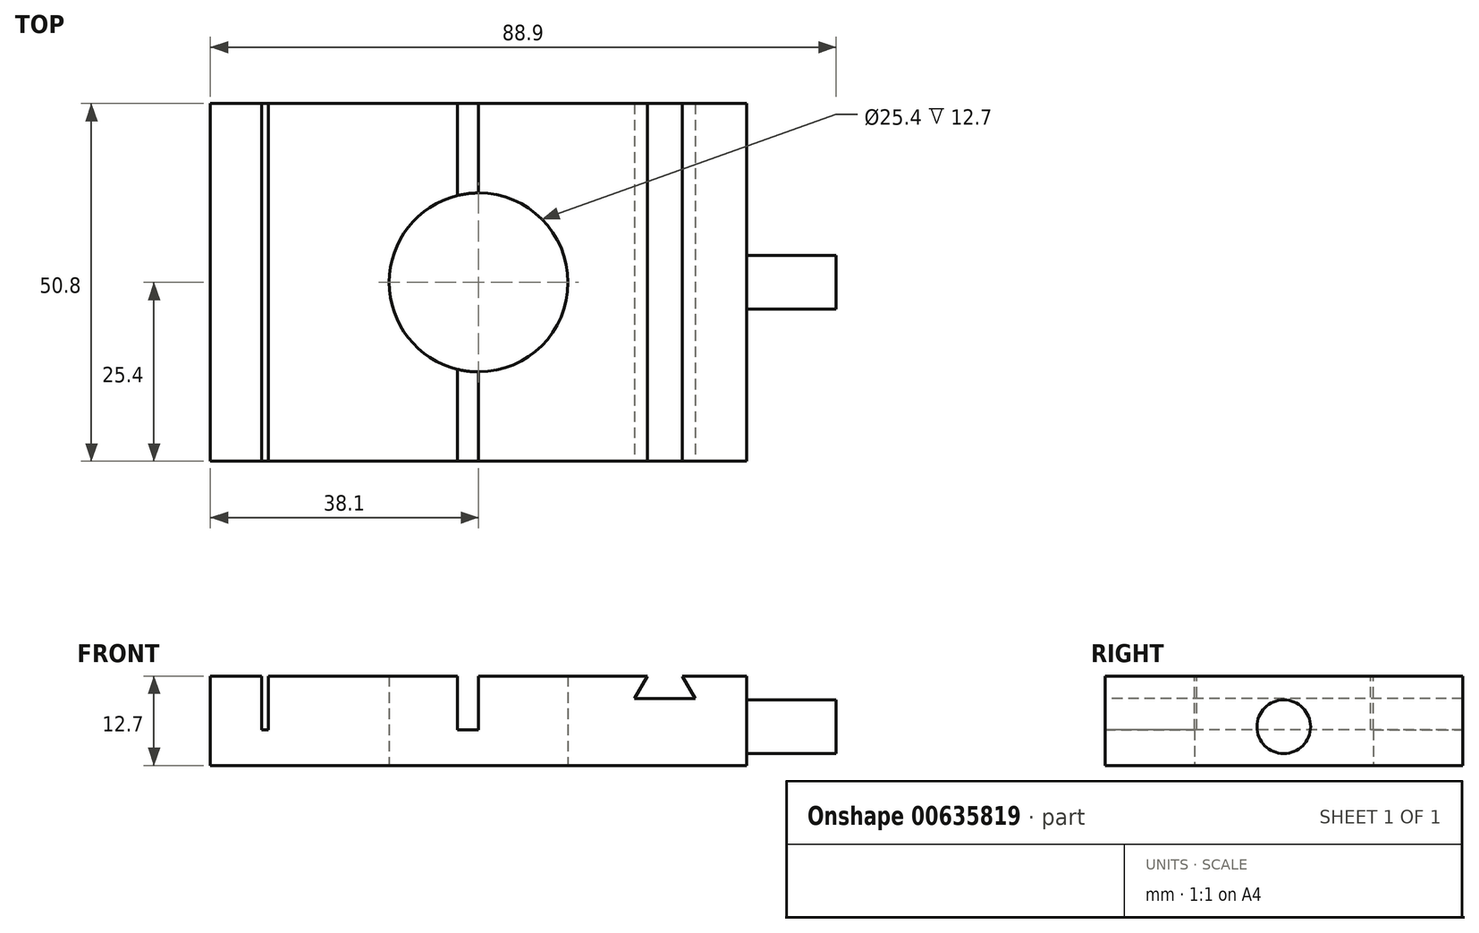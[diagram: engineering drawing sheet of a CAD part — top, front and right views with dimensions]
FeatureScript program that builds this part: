
annotation { "Feature Type Name" : "Feature", "Feature Type Description" : "" }
export const myFeature = defineFeature(function(context is Context, id is Id, definition is map)
    precondition{}
    {
        {
            var Q0;
            Q0=qCreatedBy(makeId("Top.planeOp"),FACE);
            var sketch = newSketch(context, id + "F0", { "sketchPlane" : qUnion([Q0])});
            skLineSegment(sketch, "E0.bottom", {"start": v(38.1, -25.4) * mm, "end": v(-38.1, -25.4) * mm});
            skLineSegment(sketch, "E0.top", {"start": v(38.1, 25.4) * mm, "end": v(-38.1, 25.4) * mm});
            skLineSegment(sketch, "E0.left", {"start": v(38.1, -25.4) * mm, "end": v(38.1, 25.4) * mm});
            skLineSegment(sketch, "E0.right", {"start": v(-38.1, -25.4) * mm, "end": v(-38.1, 25.4) * mm});
            skPoint(sketch, "E0.middle", {"position": v(0, 0) * mm});
            skCircle(sketch, "E1", {"center": v(0, 0) * mm, "radius": 12.7 * mm});
            skSolve(sketch);
        }
        {
            var Q0;
            Q0=makeQuery(id+"F0.imprint","IMPRINT",FACE,{"disambiguationData":[TD([[makeQuery(id+"F0.imprint","IMPRINT",EDGE,{"derivedFrom":sQuery(id+"F0.wireOp",EDGE,"E0.bottom")}),-1.0]])]});
            extrude(context, id + "F1", {"entities" : qUnion([Q0]), "depth" : 12.7 * mm, "offsetDistance" : 25.4 * mm});
        }
        {
            var Q0;
            Q0=makeQuery(id+"F1.opExtrude","CAP_FACE",FACE,{"disambiguationData":[OSD([sQuery(id+"F0.wireOp",EDGE,"E0.bottom"),sQuery(id+"F0.wireOp",EDGE,"E0.top"),sQuery(id+"F0.wireOp",EDGE,"E0.left"),sQuery(id+"F0.wireOp",EDGE,"E0.right"),sQuery(id+"F0.wireOp",EDGE,"E1")])],"isStart":false});
            var sketch = newSketch(context, id + "F2", { "sketchPlane" : qUnion([Q0])});
            skLineSegment(sketch, "E2", {"start": v(-30.83, 25.4) * mm, "end": v(-30.83, -25.4) * mm});
            skLineSegment(sketch, "E3", {"start": v(-30.83, -25.4) * mm, "end": v(-29.83, -25.4) * mm});
            skLineSegment(sketch, "E4", {"start": v(-29.83, -25.4) * mm, "end": v(-29.83, 25.4) * mm});
            skLineSegment(sketch, "E5", {"start": v(-29.83, 25.4) * mm, "end": v(-30.83, 25.4) * mm});
            skLineSegment(sketch, "E6", {"start": v(-3, 25.4) * mm, "end": v(-3, -25.4) * mm});
            skLineSegment(sketch, "E7", {"start": v(-3, -25.4) * mm, "end": v(0, -25.4) * mm});
            skLineSegment(sketch, "E8", {"start": v(0, -25.4) * mm, "end": v(0, 25.4) * mm});
            skLineSegment(sketch, "E9", {"start": v(0, 25.4) * mm, "end": v(-3, 25.4) * mm});
            skLineSegment(sketch, "E10", {"start": v(-30.33, 25.4) * mm, "end": v(-30.33, -25.4) * mm, "construction": true});
            skLineSegment(sketch, "E11", {"start": v(-1.5, 25.4) * mm, "end": v(-1.5, -25.4) * mm, "construction": true});
            skSolve(sketch);
        }
        {
            var Q0;
            Q0=makeQuery(id+"F2.imprint","IMPRINT",FACE,{"disambiguationData":[TD([[makeQuery(id+"F2.imprint","IMPRINT",EDGE,{"derivedFrom":sQuery(id+"F2.wireOp",EDGE,"E2")}),1.0]])]});
            var Q1;
            {var subQ0=sQuery(id+"F2.wireOp",EDGE,"E7");Q1=makeQuery(id+"F2.imprint","IMPRINT",FACE,{"disambiguationData":[TD([[makeQuery(id+"F2.imprint","IMPRINT",EDGE,{"derivedFrom":subQ0}),-1.0]])]});}
            var Q2;
            {var subQ0=sQuery(id+"F2.wireOp",EDGE,"E9");Q2=makeQuery(id+"F2.imprint","IMPRINT",FACE,{"disambiguationData":[TD([[makeQuery(id+"F2.imprint","IMPRINT",EDGE,{"derivedFrom":subQ0}),1.0]])]});}
            extrude(context, id + "F3", {"entities" : qUnion([Q0, Q1, Q2]), "operationType" : NewBodyOperationType.REMOVE, "oppositeDirection" : true, "depth" : 7.62 * mm, "offsetDistance" : 25.4 * mm});
        }
        {
            var Q0;
            Q0=makeQuery(id+"F1.opExtrude","SWEPT_FACE",FACE,{"disambiguationData":[OSD([sQuery(id+"F0.wireOp",EDGE,"E0.bottom")])]});
            var sketch = newSketch(context, id + "F4", { "sketchPlane" : qUnion([Q0])});
            skLineSegment(sketch, "E12", {"start": v(23.97, 12.7) * mm, "end": v(22.14, 9.53) * mm});
            skLineSegment(sketch, "E13", {"start": v(22.14, 9.53) * mm, "end": v(30.76, 9.53) * mm});
            skLineSegment(sketch, "E14", {"start": v(30.76, 9.53) * mm, "end": v(28.93, 12.7) * mm});
            skLineSegment(sketch, "E15", {"start": v(28.93, 12.7) * mm, "end": v(23.97, 12.7) * mm});
            skSolve(sketch);
        }
        {
            var Q0;
            Q0=makeQuery(id+"F4.imprint","IMPRINT",FACE,{"disambiguationData":[TD([[makeQuery(id+"F4.imprint","IMPRINT",EDGE,{"derivedFrom":sQuery(id+"F4.wireOp",EDGE,"E12")}),1.0]])]});
            extrude(context, id + "F5", {"entities" : qUnion([Q0]), "operationType" : NewBodyOperationType.REMOVE, "endBound" : BoundingType.THROUGH_ALL, "oppositeDirection" : true, "depth" : 25.4 * mm, "offsetDistance" : 25.4 * mm});
        }
        {
            var Q0;
            Q0=makeQuery(id+"F1.opExtrude","SWEPT_FACE",FACE,{"disambiguationData":[OSD([sQuery(id+"F0.wireOp",EDGE,"E0.left")])]});
            var sketch = newSketch(context, id + "F6", { "sketchPlane" : qUnion([Q0])});
            skCircle(sketch, "E16", {"center": v(0, 5.5) * mm, "radius": 3.81 * mm});
            skSolve(sketch);
        }
        {
            var Q0;
            Q0=makeQuery(id+"F6.imprint","IMPRINT",FACE,{"disambiguationData":[TD([[makeQuery(id+"F6.imprint","IMPRINT",EDGE,{"derivedFrom":sQuery(id+"F6.wireOp",EDGE,"E16")}),1.0]])]});
            extrude(context, id + "F7", {"entities" : qUnion([Q0]), "operationType" : NewBodyOperationType.ADD, "depth" : 12.7 * mm, "offsetDistance" : 25.4 * mm});
        }
    });
